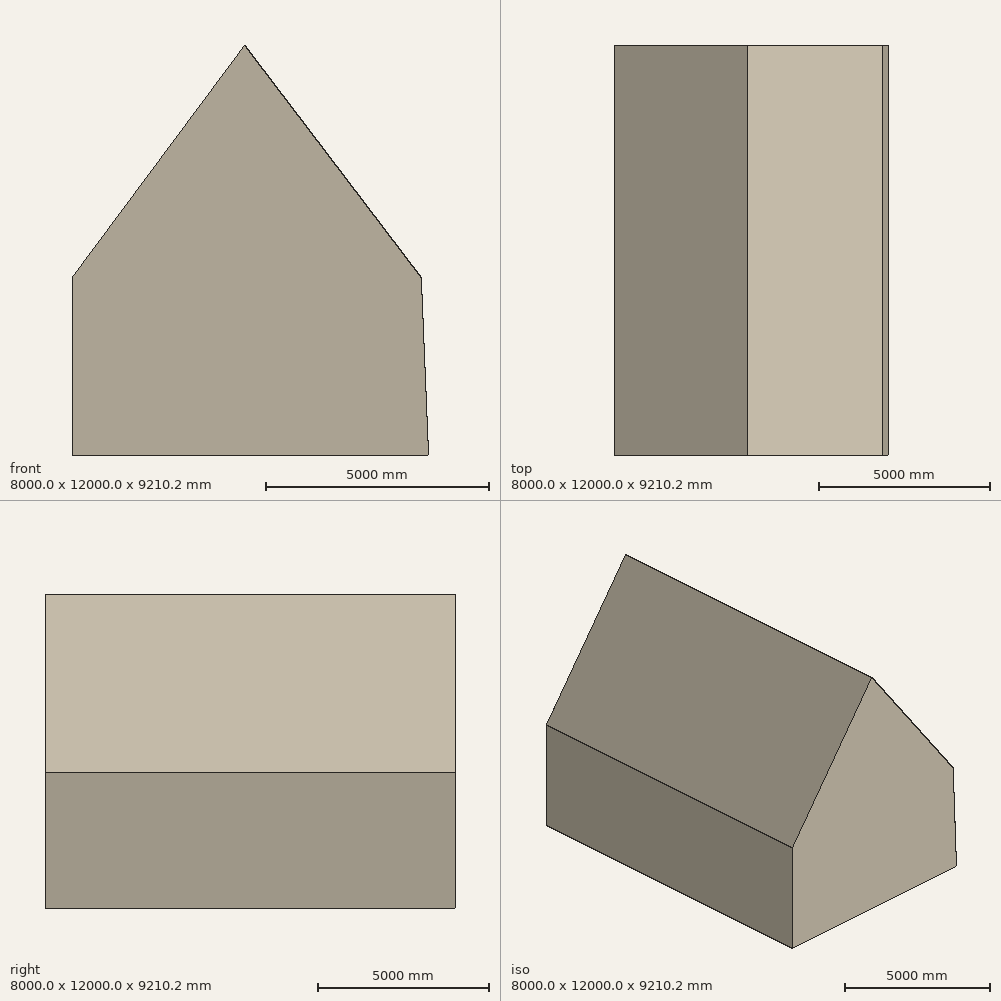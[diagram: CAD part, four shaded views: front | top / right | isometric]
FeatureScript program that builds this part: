
annotation { "Feature Type Name" : "Feature", "Feature Type Description" : "" }
export const myFeature = defineFeature(function(context is Context, id is Id, definition is map)
    precondition{}
    {
        {
            var Q0;
            Q0=qCreatedBy(makeId("Front.planeOp"),FACE);
            var sketch = newSketch(context, id + "F0", { "sketchPlane" : qUnion([Q0])});
            skLineSegment(sketch, "E0", {"start": v(0, 0) * mm, "end": v(0, 3996.66) * mm});
            skLineSegment(sketch, "E1", {"start": v(0, 3996.66) * mm, "end": v(3873.12, 9210.2) * mm});
            skLineSegment(sketch, "E2", {"start": v(3873.12, 9210.2) * mm, "end": v(7836.55, 3996.66) * mm});
            skLineSegment(sketch, "E3", {"start": v(7836.55, 3996.66) * mm, "end": v(8000, 0) * mm});
            skLineSegment(sketch, "E4", {"start": v(8000, 0) * mm, "end": v(0, 0) * mm});
            skSolve(sketch);
        }
        {
            var Q0;
            Q0=makeQuery(id+"F0.imprint","IMPRINT",FACE,{"disambiguationData":[TD([[makeQuery(id+"F0.imprint","IMPRINT",EDGE,{"derivedFrom":sQuery(id+"F0.wireOp",EDGE,"E0")}),-1.0]])]});
            extrude(context, id + "F1", {"entities" : qUnion([Q0]), "depth" : 12000 * mm});
        }
    });
